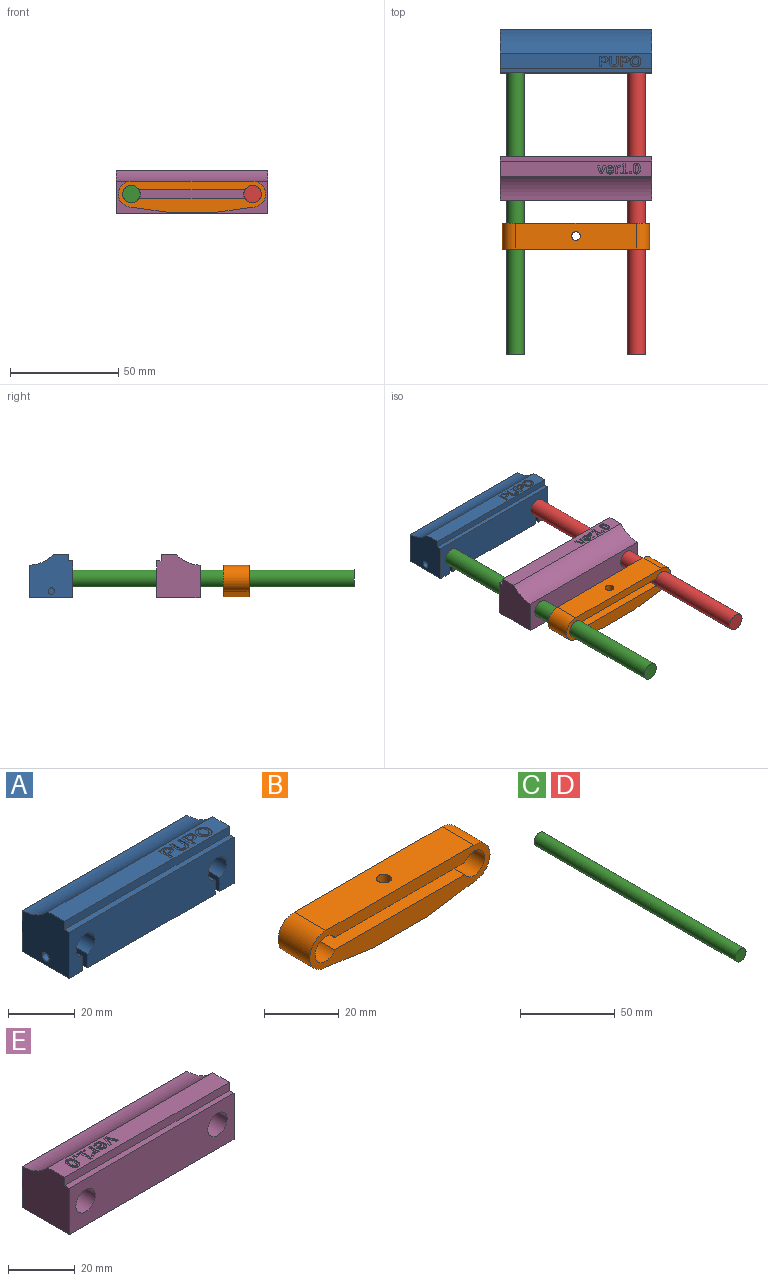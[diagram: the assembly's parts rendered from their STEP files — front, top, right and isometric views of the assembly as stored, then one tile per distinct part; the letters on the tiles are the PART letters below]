
ASSEMBLY  parts=5 mates=8
PART A: 101 faces, bbox 70x20x20 mm
  f0: plane 70x7mm, normal (0,0,1), area 433.8mm2, adj f4,f7,f9,f30,f31,f32,f33,f34
  f1: plane 70x15mm, normal (0,1,0), area 949.5mm2, adj f2,f4,f5,f6,f7,f30
  f2: plane 70x20mm, normal (0,0,-1), area 1305mm2, adj f1,f4,f7,f8,f11,f12,f13,f14
  f3: cylinder r=1.5mm len=4.62mm, axis (-1,0,0), area 43.6mm2, adj f15,f25
  f4: plane 20x20mm, normal (1,0,0), area 349.4mm2, adj f0,f1,f2,f8,f9,f10,f19,f30
  f5: cylinder r=4mm len=20mm, axis (0,1,0), area 472.3mm2, adj f1,f8,f14,f15,f16
  f6: cylinder r=4mm len=20mm, axis (0,1,0), area 472.3mm2, adj f1,f8,f11,f12,f13
  f7: plane 20x20mm, normal (-1,0,0), area 349.4mm2, adj f0,f1,f2,f8,f9,f10,f17,f30
  f8: plane 70x17mm, normal (0,-1,0), area 1069.3mm2, adj f2,f4,f5,f6,f7,f10,f11,f12
  f9: plane 70x3mm, normal (0,-1,0), area 210mm2, adj f0,f4,f7,f10
  f10: plane 70x2mm, normal (0,0,1), area 140mm2, adj f4,f7,f8,f9
  f11: plane 15x5.13mm, normal (-1,0,0), area 69.8mm2, adj f2,f6,f8,f13,f19
  f12: plane 15x5.13mm, normal (1,0,0), area 69.8mm2, adj f2,f6,f8,f13,f18
  f13: plane 5.13x2mm, normal (0,-1,0), area 10.1mm2, adj f2,f6,f11,f12
  f14: plane 15x5.16mm, normal (1,0,0), area 70.3mm2, adj f2,f5,f8,f16,f17
  f15: plane 15x5.1mm, normal (-1,0,0), area 69.4mm2, adj f2,f3,f5,f8,f16
  f16: plane 5.16x2mm, normal (0,-1,0), area 10.1mm2, adj f2,f5,f14,f15
  f17: cylinder r=1.5mm len=5.88mm, axis (-1,0,0), area 55.4mm2, adj f7,f14
  f18: cylinder r=1.5mm len=4.5mm, axis (1,0,0), area 42.4mm2, adj f12,f20
  f19: cylinder r=1.5mm len=6mm, axis (1,0,0), area 56.5mm2, adj f4,f11
  f20: plane 7x5.5mm, normal (-1,0,0), area 31.4mm2, adj f2,f18,f21,f22,f23
  f21: plane 5.5x2.5mm, normal (0,-1,0), area 13.7mm2, adj f2,f20,f23,f24
  f22: plane 5.5x2.5mm, normal (0,1,0), area 13.7mm2, adj f2,f20,f23,f24
  f23: plane 7x2.5mm, normal (0,0,-1), area 17.5mm2, adj f20,f21,f22,f24
  f24: plane 7x5.5mm, normal (1,0,0), area 38.5mm2, adj f2,f21,f22,f23
  f25: plane 7x5.5mm, normal (1,0,0), area 31.4mm2, adj f2,f3,f26,f27,f28
  f26: plane 5.5x2.5mm, normal (0,1,0), area 13.7mm2, adj f2,f25,f28,f29
  f27: plane 5.5x2.5mm, normal (0,-1,0), area 13.7mm2, adj f2,f25,f28,f29
  f28: plane 7x2.5mm, normal (0,0,-1), area 17.5mm2, adj f25,f26,f27,f29
  f29: plane 7x5.5mm, normal (-1,0,0), area 38.5mm2, adj f2,f26,f27,f28
  f30: cylinder r=15.45mm len=70mm, axis (-1,0,0), area 869mm2, adj f0,f1,f4,f7
  f31: extruded ~1.52x0.49mm, area 0.7mm2, adj f0,f32,f44,f45
  f32: extruded ~1.59x0.5mm, area 0.7mm2, adj f0,f31,f33,f45
  f33: extruded ~1.42x0.56mm, area 0.6mm2, adj f0,f32,f34,f45
  f34: plane 2.96x0.4mm, normal (-1,0,0), area 1.2mm2, adj f0,f33,f35,f45
  f35: plane 1.01x0.4mm, normal (0,-1,0), area 0.4mm2, adj f0,f34,f36,f45
  f36: plane 2.89x0.4mm, normal (1,0,0), area 1.2mm2, adj f0,f35,f37,f45
  f37: extruded ~0.89x0.4mm, area 0.4mm2, adj f0,f36,f38,f45
  f38: extruded ~0.83x0.4mm, area 0.4mm2, adj f0,f37,f39,f45
  f39: extruded ~0.8x0.4mm, area 0.4mm2, adj f0,f38,f40,f45
  f40: extruded ~0.87x0.4mm, area 0.4mm2, adj f0,f39,f41,f45
  f41: plane 2.93x0.4mm, normal (-1,0,0), area 1.2mm2, adj f0,f40,f42,f45
  f42: plane 1.01x0.4mm, normal (0,-1,0), area 0.4mm2, adj f0,f41,f43,f45
  f43: plane 3.01x0.4mm, normal (1,0,0), area 1.2mm2, adj f0,f42,f44,f45
  f44: extruded ~1.39x0.53mm, area 0.6mm2, adj f0,f31,f43,f45
  f45: plane 4.88x4.2mm, normal (0,0,1), area 10.6mm2, adj f31,f32,f33,f34,f35,f36,f37,f38
  f46: extruded ~0.89x0.76mm, area 0.5mm2, adj f47,f61,f62,f98
  f47: extruded ~0.6x0.4mm, area 0.3mm2, adj f46,f48,f62,f98
  f48: extruded ~0.64x0.4mm, area 0.3mm2, adj f47,f49,f62,f98
  f49: plane 1.07x0.4mm, normal (0,-1,0), area 0.4mm2, adj f48,f50,f62,f98
  f50: plane 1.56x0.4mm, normal (-1,0,0), area 0.6mm2, adj f49,f61,f62,f98
  f51: extruded ~0.83x0.4mm, area 0.3mm2, adj f0,f52,f60,f62
  f52: extruded ~1.13x0.47mm, area 0.5mm2, adj f0,f51,f53,f62
  f53: extruded ~1.33x0.4mm, area 0.6mm2, adj f0,f52,f54,f62
  f54: plane 2.16x0.4mm, normal (0,-1,0), area 0.9mm2, adj f0,f53,f55,f62
  f55: plane 4.81x0.4mm, normal (1,0,0), area 1.9mm2, adj f0,f54,f56,f62
  f56: plane 1.01x0.4mm, normal (0,1,0), area 0.4mm2, adj f0,f55,f57,f62
  f57: plane 1.69x0.4mm, normal (-1,0,0), area 0.7mm2, adj f0,f56,f58,f62
  f58: plane 1.19x0.4mm, normal (0,1,0), area 0.5mm2, adj f0,f57,f59,f62
  f59: extruded ~0.94x0.4mm, area 0.4mm2, adj f0,f58,f60,f62
  f60: extruded ~0.61x0.56mm, area 0.3mm2, adj f0,f51,f59,f62
  f61: plane 1.04x0.4mm, normal (0,1,0), area 0.4mm2, adj f46,f50,f62,f98
  f62: plane 4.81x3.96mm, normal (0,0,1), area 10.2mm2, adj f46,f47,f48,f49,f50,f51,f52,f53
  f63: extruded ~0.89x0.76mm, area 0.5mm2, adj f64,f78,f79,f99
  f64: extruded ~0.6x0.4mm, area 0.3mm2, adj f63,f65,f79,f99
  f65: extruded ~0.64x0.4mm, area 0.3mm2, adj f64,f66,f79,f99
  f66: plane 1.07x0.4mm, normal (0,-1,0), area 0.4mm2, adj f65,f67,f79,f99
  f67: plane 1.56x0.4mm, normal (-1,0,0), area 0.6mm2, adj f66,f78,f79,f99
  f68: extruded ~0.83x0.4mm, area 0.3mm2, adj f0,f69,f77,f79
  f69: extruded ~1.13x0.47mm, area 0.5mm2, adj f0,f68,f70,f79
  f70: extruded ~1.33x0.4mm, area 0.6mm2, adj f0,f69,f71,f79
  f71: plane 2.16x0.4mm, normal (0,-1,0), area 0.9mm2, adj f0,f70,f72,f79
  f72: plane 4.81x0.4mm, normal (1,0,0), area 1.9mm2, adj f0,f71,f73,f79
  f73: plane 1.01x0.4mm, normal (0,1,0), area 0.4mm2, adj f0,f72,f74,f79
  f74: plane 1.69x0.4mm, normal (-1,0,0), area 0.7mm2, adj f0,f73,f75,f79
  f75: plane 1.19x0.4mm, normal (0,1,0), area 0.5mm2, adj f0,f74,f76,f79
  f76: extruded ~0.94x0.4mm, area 0.4mm2, adj f0,f75,f77,f79
  f77: extruded ~0.61x0.56mm, area 0.3mm2, adj f0,f68,f76,f79
  f78: plane 1.04x0.4mm, normal (0,1,0), area 0.4mm2, adj f63,f67,f79,f99
  f79: plane 4.81x3.96mm, normal (0,0,1), area 10.2mm2, adj f63,f64,f65,f66,f67,f68,f69,f70
  f80: extruded ~1.22x0.4mm, area 0.5mm2, adj f81,f96,f97,f100
  f81: extruded ~1.26x0.4mm, area 0.5mm2, adj f80,f82,f97,f100
  f82: extruded ~1.04x0.44mm, area 0.5mm2, adj f81,f83,f97,f100
  f83: extruded ~1.03x0.46mm, area 0.5mm2, adj f82,f84,f97,f100
  f84: extruded ~1.25x0.4mm, area 0.5mm2, adj f83,f85,f97,f100
  f85: extruded ~1.22x0.4mm, area 0.5mm2, adj f84,f86,f97,f100
  f86: extruded ~1.04x0.44mm, area 0.5mm2, adj f85,f96,f97,f100
  f87: extruded ~1.32x0.4mm, area 0.5mm2, adj f0,f88,f95,f97
  f88: extruded ~1.8x0.64mm, area 0.8mm2, adj f0,f87,f89,f97
  f89: extruded ~1.79x0.66mm, area 0.8mm2, adj f0,f88,f90,f97
  f90: extruded ~1.78x0.65mm, area 0.8mm2, adj f0,f89,f91,f97
  f91: extruded ~1.81x0.64mm, area 0.8mm2, adj f0,f90,f92,f97
  f92: extruded ~1.83x0.64mm, area 0.8mm2, adj f0,f91,f93,f97
  f93: extruded ~1.78x0.67mm, area 0.8mm2, adj f0,f92,f94,f97
  f94: extruded ~1.29x0.4mm, area 0.5mm2, adj f0,f93,f95,f97
  f95: extruded ~0.87x0.85mm, area 0.5mm2, adj f0,f87,f94,f97
  f96: extruded ~1.03x0.44mm, area 0.5mm2, adj f80,f86,f97,f100
  f97: plane 4.95x4.86mm, normal (0,0,1), area 11.8mm2, adj f80,f81,f82,f83,f84,f85,f86,f87
  f98: plane 1.94x1.56mm, normal (0,0,1), area 2.8mm2, adj f46,f47,f48,f49,f50,f61
  f99: plane 1.94x1.56mm, normal (0,0,1), area 2.8mm2, adj f63,f64,f65,f66,f67,f78
  f100: plane 3.36x2.82mm, normal (0,0,1), area 7.8mm2, adj f80,f81,f82,f83,f84,f85,f86,f96
PART B: 21 faces, bbox 68x12x14.6 mm
  f0: cylinder r=2mm len=4mm, axis (0,0,1), area 32.1mm2, adj f10,f14
  f1: cylinder r=4mm len=12mm, axis (0,1,0), area 251.3mm2, adj f2,f10,f11,f12
  f2: plane 49.07x12mm, normal (0,0,-1), area 576.3mm2, adj f1,f3,f11,f12,f13
  f3: cylinder r=4mm len=12mm, axis (0,1,0), area 251.3mm2, adj f2,f10,f11,f12
  f4: plane 55.85x12mm, normal (0,0,1), area 657.6mm2, adj f5,f9,f11,f12,f13
  f5: cylinder r=6mm len=12mm, axis (0,1,0), area 227.5mm2, adj f4,f6,f11,f12
  f6: plane 17.97x12mm, normal (-0.14,0,-0.99), area 217.8mm2, adj f5,f7,f11,f12
  f7: plane 20x12mm, normal (0,0,-1), area 208.8mm2, adj f6,f8,f11,f12,f15,f16,f17,f18
  f8: plane 18x12mm, normal (0.14,0,-0.99), area 218.2mm2, adj f7,f9,f11,f12
  f9: cylinder r=6mm len=12mm, axis (0,1,0), area 227.1mm2, adj f4,f8,f11,f12
  f10: plane 49.07x12mm, normal (0,0,1), area 576.3mm2, adj f0,f1,f3,f11,f12
  f11: plane 68x14.56mm, normal (0,-1,0), area 588.3mm2, adj f1,f2,f3,f4,f5,f6,f7,f8
  f12: plane 68x14.56mm, normal (0,1,0), area 588.3mm2, adj f1,f2,f3,f4,f5,f6,f7,f8
  f13: cylinder r=2mm len=4mm, axis (0,0,1), area 50.3mm2, adj f2,f4
  f14: plane 6.93x6mm, normal (0,0,-1), area 18.6mm2, adj f0,f15,f16,f17,f18,f19,f20
  f15: plane 4x3mm, normal (0.87,-0.5,0), area 13.9mm2, adj f7,f14,f16,f20
  f16: plane 4x3.46mm, normal (0,-1,0), area 13.9mm2, adj f7,f14,f15,f17
  f17: plane 4x3mm, normal (-0.87,-0.5,0), area 13.9mm2, adj f7,f14,f16,f18
  f18: plane 4x3mm, normal (-0.87,0.5,0), area 13.9mm2, adj f7,f14,f17,f19
  f19: plane 4x3.46mm, normal (0,1,0), area 13.9mm2, adj f7,f14,f18,f20
  f20: plane 4x3mm, normal (0.87,0.5,0), area 13.9mm2, adj f7,f14,f15,f19
PART C: 3 faces, bbox 8x150x8 mm
  f0: cylinder r=4mm len=150mm, axis (0,1,0), area 3769.9mm2, adj f1,f2
  f1: plane 8x8mm, normal (0,-1,0), area 50.3mm2, adj f0
  f2: plane 8x8mm, normal (0,1,0), area 50.3mm2, adj f0
PART D: same geometry as C
PART E: 98 faces, bbox 70x20x20 mm
  f0: plane 70x7mm, normal (0,0,1), area 448.3mm2, adj f3,f6,f8,f10,f22,f23,f24,f25
  f1: plane 70x15mm, normal (0,1,0), area 944.4mm2, adj f2,f3,f4,f5,f6,f10
  f2: plane 70x20mm, normal (0,0,-1), area 1400mm2, adj f1,f3,f6,f7
  f3: plane 20x20mm, normal (1,0,0), area 356.5mm2, adj f0,f1,f2,f7,f8,f9,f10
  f4: cylinder r=4.1mm len=20mm, axis (0,1,0), area 515.2mm2, adj f1,f7
  f5: cylinder r=4.1mm len=20mm, axis (0,1,0), area 515.2mm2, adj f1,f7
  f6: plane 20x20mm, normal (-1,0,0), area 356.5mm2, adj f0,f1,f2,f7,f8,f9,f10
  f7: plane 70x17mm, normal (0,-1,0), area 1084.4mm2, adj f2,f3,f4,f5,f6,f9
  f8: plane 70x3mm, normal (0,-1,0), area 210mm2, adj f0,f3,f6,f9
  f9: plane 70x2mm, normal (0,0,1), area 140mm2, adj f3,f6,f7,f8
  f10: cylinder r=15.45mm len=70mm, axis (-1,0,0), area 869mm2, adj f0,f1,f3,f6
  f11: extruded ~1.03x0.4mm, area 0.4mm2, adj f12,f30,f31,f96
  f12: extruded ~1.01x0.4mm, area 0.4mm2, adj f11,f13,f31,f96
  f13: extruded ~0.54x0.4mm, area 0.2mm2, adj f12,f14,f31,f96
  f14: extruded ~0.42x0.4mm, area 0.2mm2, adj f13,f15,f31,f96
  f15: extruded ~0.42x0.4mm, area 0.2mm2, adj f14,f16,f31,f96
  f16: extruded ~0.53x0.4mm, area 0.2mm2, adj f15,f17,f31,f96
  f17: extruded ~1.03x0.4mm, area 0.4mm2, adj f16,f18,f31,f96
  f18: extruded ~1.03x0.4mm, area 0.4mm2, adj f17,f19,f31,f96
  f19: extruded ~0.53x0.4mm, area 0.2mm2, adj f18,f20,f31,f96
  f20: extruded ~0.44x0.4mm, area 0.2mm2, adj f19,f21,f31,f96
  f21: extruded ~0.42x0.4mm, area 0.2mm2, adj f20,f30,f31,f96
  f22: extruded ~1.85x0.42mm, area 0.8mm2, adj f0,f23,f29,f31
  f23: extruded ~1.86x0.4mm, area 0.8mm2, adj f0,f22,f24,f31
  f24: extruded ~1.25x0.62mm, area 0.6mm2, adj f0,f23,f25,f31
  f25: extruded ~0.96x0.4mm, area 0.4mm2, adj f0,f24,f26,f31
  f26: extruded ~0.81x0.54mm, area 0.4mm2, adj f0,f25,f27,f31
  f27: extruded ~1.41x0.4mm, area 0.6mm2, adj f0,f26,f28,f31
  f28: extruded ~2.47x1.65mm, area 1.4mm2, adj f0,f27,f29,f31
  f29: extruded ~1.25x0.63mm, area 0.6mm2, adj f0,f22,f28,f31
  f30: extruded ~0.53x0.4mm, area 0.2mm2, adj f11,f21,f31,f96
  f31: plane 4.95x3.32mm, normal (0,0,1), area 9.6mm2, adj f11,f12,f13,f14,f15,f16,f17,f18
  f32: plane 2.83x0.4mm, normal (-1,0,0), area 1.1mm2, adj f0,f33,f48,f49
  f33: plane 0.96x0.4mm, normal (0,-1,0), area 0.4mm2, adj f0,f32,f34,f49
  f34: plane 1.81x0.4mm, normal (1,0,0), area 0.7mm2, adj f0,f33,f35,f49
  f35: extruded ~0.86x0.4mm, area 0.4mm2, adj f0,f34,f36,f49
  f36: extruded ~0.56x0.4mm, area 0.3mm2, adj f0,f35,f37,f49
  f37: extruded ~0.41x0.4mm, area 0.2mm2, adj f0,f36,f38,f49
  f38: plane 0.8x0.4mm, normal (1,0,0), area 0.3mm2, adj f0,f37,f39,f49
  f39: extruded ~0.4x0.3mm, area 0.1mm2, adj f0,f38,f40,f49
  f40: extruded ~0.4x0.38mm, area 0.2mm2, adj f0,f39,f41,f49
  f41: extruded ~0.4x0.26mm, area 0.1mm2, adj f0,f40,f42,f49
  f42: extruded ~0.55x0.4mm, area 0.2mm2, adj f0,f41,f43,f49
  f43: plane 0.4x0.01mm, normal (0,1,0), area 0mm2, adj f0,f42,f44,f49
  f44: extruded ~0.42x0.4mm, area 0.2mm2, adj f0,f43,f45,f49
  f45: extruded ~0.4x0.37mm, area 0.1mm2, adj f0,f44,f46,f49
  f46: plane 0.91x0.4mm, normal (0,1,0), area 0.4mm2, adj f0,f45,f47,f49
  f47: extruded ~0.4x0.36mm, area 0.1mm2, adj f0,f46,f48,f49
  f48: extruded ~0.51x0.4mm, area 0.2mm2, adj f0,f32,f47,f49
  f49: plane 3.76x2.15mm, normal (0,0,1), area 4.4mm2, adj f32,f33,f34,f35,f36,f37,f38,f39
  f50: plane 0.71x0.4mm, normal (-1,0,0), area 0.3mm2, adj f0,f51,f60,f61
  f51: plane 3.25x0.4mm, normal (0,-1,0), area 1.3mm2, adj f0,f50,f52,f61
  f52: plane 0.71x0.4mm, normal (1,0,0), area 0.3mm2, adj f0,f51,f53,f61
  f53: plane 1.1x0.4mm, normal (0,1,0), area 0.4mm2, adj f0,f52,f54,f61
  f54: plane 4.1x0.4mm, normal (1,0,0), area 1.6mm2, adj f0,f53,f55,f61
  f55: plane 0.91x0.4mm, normal (0,1,0), area 0.4mm2, adj f0,f54,f56,f61
  f56: plane 1.2x0.78mm, normal (-0.54,0.84,0), area 0.6mm2, adj f0,f55,f57,f61
  f57: plane 0.75x0.4mm, normal (-1,0,0), area 0.3mm2, adj f0,f56,f58,f61
  f58: plane 1.15x0.72mm, normal (0.53,-0.85,0), area 0.5mm2, adj f0,f57,f59,f61
  f59: plane 3.28x0.4mm, normal (-1,0,0), area 1.3mm2, adj f0,f58,f60,f61
  f60: plane 1.19x0.4mm, normal (0,1,0), area 0.5mm2, adj f0,f50,f59,f61
  f61: plane 4.81x3.25mm, normal (0,0,1), area 7.1mm2, adj f50,f51,f52,f53,f54,f55,f56,f57
  f62: plane 1.04x0.4mm, normal (-1,0,0), area 0.4mm2, adj f0,f63,f65,f66
  f63: plane 0.99x0.4mm, normal (0,-1,0), area 0.4mm2, adj f0,f62,f64,f66
  f64: plane 1.04x0.4mm, normal (1,0,0), area 0.4mm2, adj f0,f63,f65,f66
  f65: plane 0.99x0.4mm, normal (0,1,0), area 0.4mm2, adj f0,f62,f64,f66
  f66: plane 1.04x0.99mm, normal (0,0,1), area 1mm2, adj f62,f63,f64,f65
  f67: extruded ~0.52x0.4mm, area 0.2mm2, adj f68,f84,f85,f97
  f68: extruded ~0.51x0.4mm, area 0.2mm2, adj f67,f69,f85,f97
  f69: extruded ~0.67x0.4mm, area 0.3mm2, adj f68,f70,f85,f97
  f70: plane 1.43x0.4mm, normal (0,1,0), area 0.6mm2, adj f69,f84,f85,f97
  f71: extruded ~1.28x0.49mm, area 0.6mm2, adj f0,f72,f83,f85
  f72: extruded ~1.59x1mm, area 0.8mm2, adj f0,f71,f73,f85
  f73: plane 0.9x0.4mm, normal (0.09,1,0), area 0.4mm2, adj f0,f72,f74,f85
  f74: extruded ~0.64x0.44mm, area 0.3mm2, adj f0,f73,f75,f85
  f75: extruded ~0.57x0.4mm, area 0.3mm2, adj f0,f74,f76,f85
  f76: extruded ~0.81x0.4mm, area 0.3mm2, adj f0,f75,f77,f85
  f77: plane 2.37x0.4mm, normal (0,-1,0), area 0.9mm2, adj f0,f76,f78,f85
  f78: plane 0.4x0.03mm, normal (1,0,0), area 0mm2, adj f0,f77,f79,f85
  f79: extruded ~1.54x0.42mm, area 0.7mm2, adj f0,f78,f80,f85
  f80: extruded ~1.22x0.53mm, area 0.5mm2, adj f0,f79,f81,f85
  f81: extruded ~1.29x0.49mm, area 0.6mm2, adj f0,f80,f82,f85
  f82: extruded ~1.41x0.45mm, area 0.6mm2, adj f0,f81,f83,f85
  f83: extruded ~1.44x0.45mm, area 0.6mm2, adj f0,f71,f82,f85
  f84: extruded ~0.66x0.4mm, area 0.3mm2, adj f67,f70,f85,f97
  f85: plane 3.83x3.38mm, normal (0,0,1), area 7.7mm2, adj f67,f68,f69,f70,f71,f72,f73,f74
  f86: plane 1.15x0.4mm, normal (0,-1,0), area 0.5mm2, adj f0,f87,f94,f95
  f87: plane 3.69x1.36mm, normal (0.94,-0.35,0), area 1.6mm2, adj f0,f86,f88,f95
  f88: plane 1x0.4mm, normal (0,1,0), area 0.4mm2, adj f0,f87,f89,f95
  f89: extruded ~2.43x0.79mm, area 1mm2, adj f0,f88,f90,f95
  f90: extruded ~0.49x0.4mm, area 0.2mm2, adj f0,f89,f91,f95
  f91: extruded ~0.85x0.4mm, area 0.4mm2, adj f0,f90,f92,f95
  f92: plane 2.06x0.65mm, normal (0.95,0.3,0), area 0.9mm2, adj f0,f91,f93,f95
  f93: plane 1.01x0.4mm, normal (0,1,0), area 0.4mm2, adj f0,f92,f94,f95
  f94: plane 3.69x1.32mm, normal (-0.94,-0.34,0), area 1.6mm2, adj f0,f86,f93,f95
  f95: plane 3.83x3.69mm, normal (0,0,1), area 6.6mm2, adj f86,f87,f88,f89,f90,f91,f92,f93
  f96: plane 3.44x1.4mm, normal (0,0,1), area 4.2mm2, adj f11,f12,f13,f14,f15,f16,f17,f18
  f97: plane 1.43x0.89mm, normal (0,0,1), area 1mm2, adj f67,f68,f69,f70,f84
PLACE A t=(0.51,61.44,1.96)mm fixed
PLACE B t=(0.51,-27.92,0.96)mm
PLACE C t=(-27.49,61.44,0.96)mm
PLACE D t=(28.51,61.44,0.96)mm
PLACE E rot(axis=(0,0,1),180deg) t=(0.51,-17.27,1.96)mm
MATE cylindrical B.f1 <-> C.f0  axis (0,1,0) through (-27.49,-39.92,0.96)mm
MATE cylindrical E.f5 <-> C.f0  axis (0,-1,0) through (-27.49,-17.27,0.96)mm
MATE cylindrical A.f6 <-> D.f0  axis (0,1,0) through (28.51,61.44,0.96)mm
MATE planar A.f1 <-> C.f0  axis (0,1,0) through (0.51,61.44,-0.7)mm
MATE planar A.f1 <-> D.f0  axis (0,1,0) through (0.51,61.44,-0.7)mm
MATE cylindrical B.f3 <-> D.f0  axis (0,-1,0) through (28.51,-39.92,0.96)mm
MATE cylindrical A.f5 <-> C.f0  axis (0,-1,0) through (-27.49,41.44,0.96)mm
MATE cylindrical E.f4 <-> D.f0  axis (0,-1,0) through (28.51,-17.27,0.96)mm
